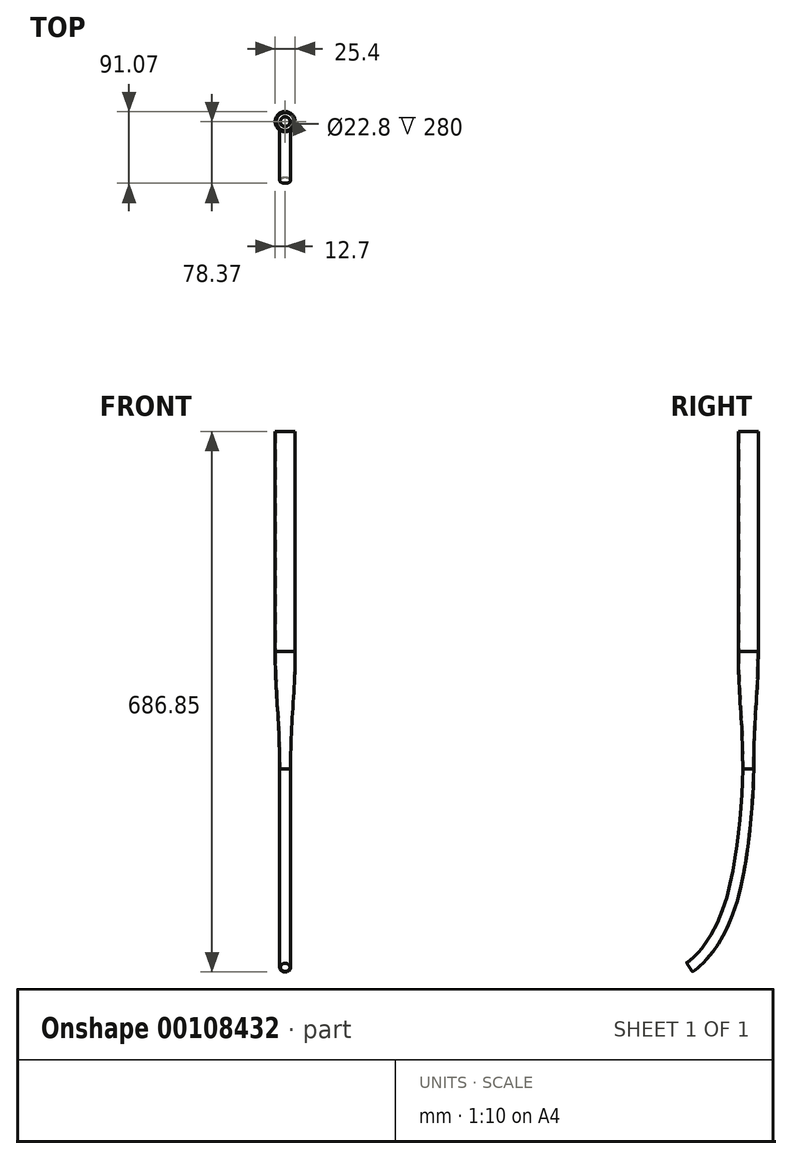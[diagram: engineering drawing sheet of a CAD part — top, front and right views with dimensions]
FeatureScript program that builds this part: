
annotation { "Feature Type Name" : "Feature", "Feature Type Description" : "" }
export const myFeature = defineFeature(function(context is Context, id is Id, definition is map)
    precondition{}
    {
        {
            var Q0;
            Q0=qCreatedBy(makeId("Right.planeOp"),FACE);
            var sketch = newSketch(context, id + "F0", { "sketchPlane" : qUnion([Q0])});
            skLineSegment(sketch, "E0.bottom", {"start": v(11.4, 429) * mm, "end": v(12.7, 429) * mm});
            skLineSegment(sketch, "E0.top", {"start": v(11.4, 149) * mm, "end": v(12.7, 149) * mm});
            skLineSegment(sketch, "E0.left", {"start": v(11.4, 429) * mm, "end": v(11.4, 149) * mm});
            skLineSegment(sketch, "E0.right", {"start": v(12.7, 429) * mm, "end": v(12.7, 149) * mm});
            skLineSegment(sketch, "E1", {"start": v(6.1, 0) * mm, "end": v(7, 0) * mm});
            skFitSpline(sketch, "E2", {"points": [v(12.7, 149) * mm, v(7, 0) * mm], "startDerivative": vector(0, -170.14) * mm, "endDerivative": vector(0, -200) * mm});
            skFitSpline(sketch, "E3", {"points": [v(11.4, 149) * mm, v(6.1, 0) * mm], "startDerivative": vector(0, -169.63) * mm, "endDerivative": vector(0, -199.89) * mm});
            skLineSegment(sketch, "E4", {"start": v(6.1, 0) * mm, "end": v(0, 0) * mm});
            skLineSegment(sketch, "E5", {"start": v(0, 0) * mm, "end": v(0, 429) * mm});
            skLineSegment(sketch, "E6", {"start": v(0, 429) * mm, "end": v(11.4, 429) * mm});
            skSolve(sketch);
        }
        {
            var Q0;
            Q0=makeQuery(id+"F0.imprint","IMPRINT",FACE,{"disambiguationData":[TD([[makeQuery(id+"F0.imprint","IMPRINT",EDGE,{"derivedFrom":sQuery(id+"F0.wireOp",EDGE,"E0.bottom")}),-1.0]])]});
            var Q1;
            Q1=makeQuery(id+"F0.imprint","IMPRINT",FACE,{"disambiguationData":[TD([[makeQuery(id+"F0.imprint","IMPRINT",EDGE,{"derivedFrom":sQuery(id+"F0.wireOp",EDGE,"E0.top")}),-1.0]])]});
            var Q2;
            Q2=sQuery(id+"F0.wireOp",EDGE,"E5");
            revolve(context, id + "F1", {"entities" : qUnion([Q0, Q1]), "axis" : qUnion([Q2]), "revolveType" : RevolveType.FULL});
        }
        {
            var Q0;
            Q0=qCreatedBy(makeId("Top.planeOp"),FACE);
            var sketch = newSketch(context, id + "F2", { "sketchPlane" : qUnion([Q0])});
            skCircle(sketch, "E7", {"center": v(0, 0) * mm, "radius": 7 * mm});
            skCircle(sketch, "E8", {"center": v(0, 0) * mm, "radius": 6.1 * mm});
            skSolve(sketch);
        }
        {
            var Q0;
            Q0=qCreatedBy(makeId("Right.planeOp"),FACE);
            var sketch = newSketch(context, id + "F3", { "sketchPlane" : qUnion([Q0])});
            skFitSpline(sketch, "E9", {"points": [v(0, 0) * mm, v(-24.09, -176.33) * mm, v(-74.59, -251.96) * mm], "startDerivative": vector(0, -134.78) * mm, "endDerivative": vector(-106.22, -68.27) * mm});
            skSolve(sketch);
        }
        {
            var Q0;
            Q0 = qSketchRegion(id + "F2", true);
            var Q1;
            Q1 = qConstructionFilter(qBodyType(qCreatedBy(id + "F3" ,EDGE), BodyType.WIRE), ConstructionObject.NO);
            sweep(context, id + "F4", {"operationType" : NewBodyOperationType.ADD, "profiles" : qUnion([Q0]), "path" : qUnion([Q1])});
        }
    });
